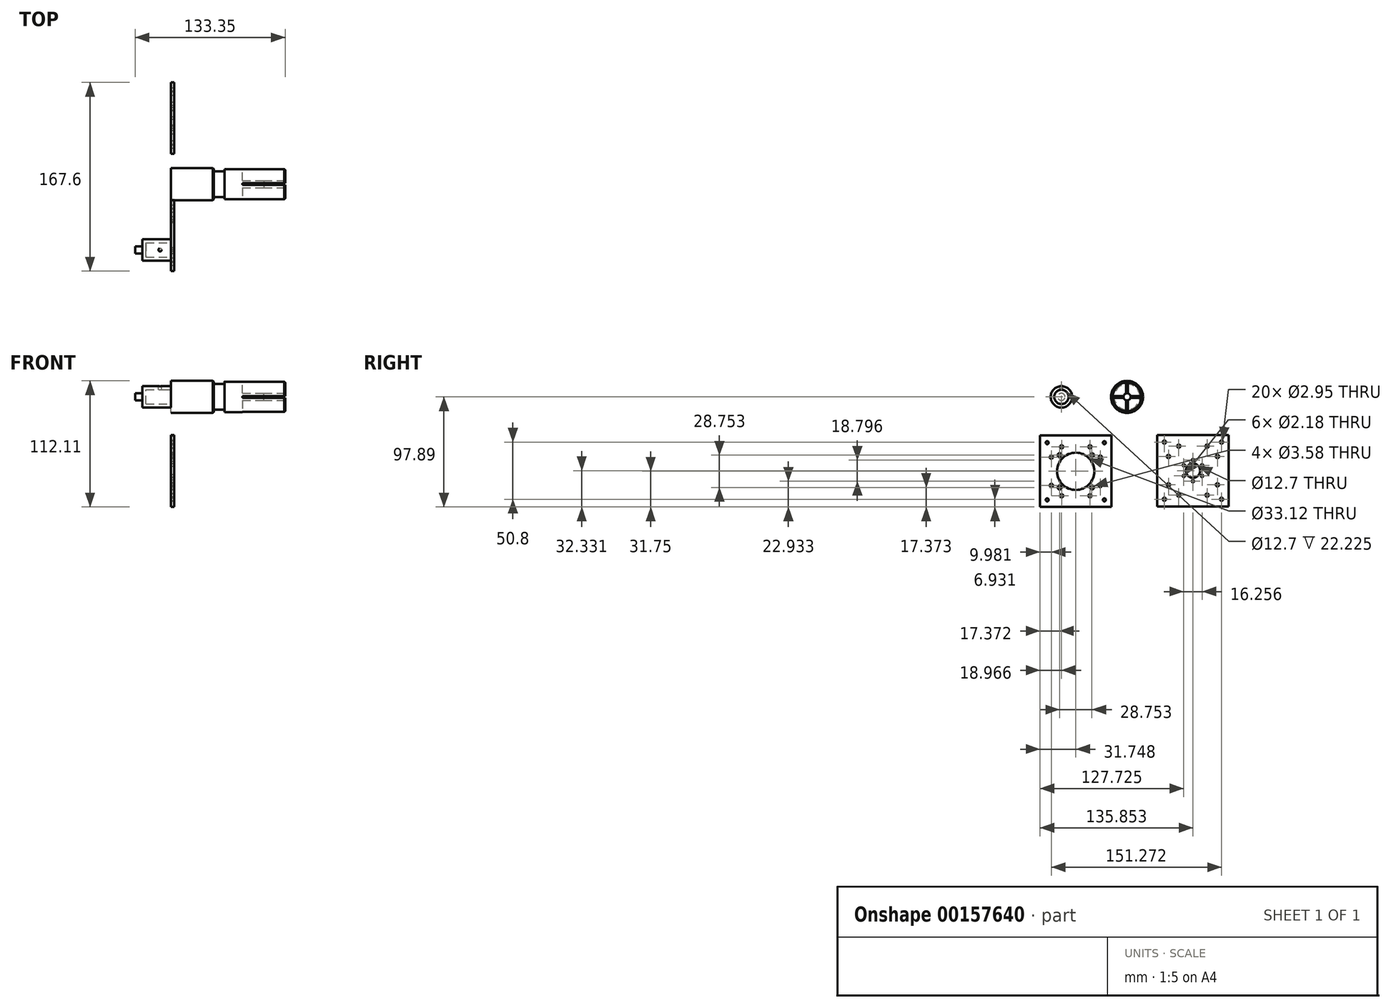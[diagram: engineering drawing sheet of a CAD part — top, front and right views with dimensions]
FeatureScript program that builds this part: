
annotation { "Feature Type Name" : "Feature", "Feature Type Description" : "" }
export const myFeature = defineFeature(function(context is Context, id is Id, definition is map)
    precondition{}
    {
        {
            var Q0;
            Q0=qCreatedBy(makeId("Right.planeOp"),FACE);
            var sketch = newSketch(context, id + "F0", { "sketchPlane" : qUnion([Q0])});
            skCircle(sketch, "E0", {"center": v(0, 0) * mm, "radius": 14.22 * mm});
            skSolve(sketch);
        }
        {
            var Q0;
            Q0=makeQuery(id+"F0.imprint","IMPRINT",FACE,{"disambiguationData":[TD([[makeQuery(id+"F0.imprint","IMPRINT",EDGE,{"derivedFrom":sQuery(id+"F0.wireOp",EDGE,"E0")}),1.0]])]});
            extrude(context, id + "F1", {"entities" : qUnion([Q0]), "depth" : 38.1 * mm});
        }
        {
            var Q0;
            Q0=makeQuery(id+"F1.opExtrude","CAP_FACE",FACE,{"disambiguationData":[OSD([sQuery(id+"F0.wireOp",EDGE,"E0")])],"isStart":false});
            var sketch = newSketch(context, id + "F2", { "sketchPlane" : qUnion([Q0])});
            skCircle(sketch, "E1", {"center": v(0, 0) * mm, "radius": 11.43 * mm});
            skSolve(sketch);
        }
        {
            var Q0;
            Q0=makeQuery(id+"F2.imprint","IMPRINT",FACE,{"disambiguationData":[TD([[makeQuery(id+"F2.imprint","IMPRINT",EDGE,{"derivedFrom":sQuery(id+"F2.wireOp",EDGE,"E1")}),1.0]])]});
            extrude(context, id + "F3", {"entities" : qUnion([Q0]), "operationType" : NewBodyOperationType.ADD, "depth" : 9.65 * mm});
        }
        {
            var Q0;
            Q0=makeQuery(id+"F3.opExtrude","CAP_FACE",FACE,{"disambiguationData":[OSD([sQuery(id+"F2.wireOp",EDGE,"E1")])],"isStart":false});
            var sketch = newSketch(context, id + "F4", { "sketchPlane" : qUnion([Q0])});
            skCircle(sketch, "E2", {"center": v(0, 0) * mm, "radius": 13.45 * mm});
            skSolve(sketch);
        }
        {
            var Q0;
            Q0=makeQuery(id+"F4.imprint","IMPRINT",FACE,{"disambiguationData":[TD([[makeQuery(id+"F4.imprint","IMPRINT",EDGE,{"derivedFrom":sQuery(id+"F4.wireOp",EDGE,"E2")}),1.0]])]});
            var Q1;
            Q1=makeQuery(id+"F4.imprint","IMPRINT",FACE,{"disambiguationData":[TD([[makeQuery(id+"F4.imprint","IMPRINT",EDGE,{"derivedFrom":makeQuery(id+"F3.opExtrude","CAP_EDGE",EDGE,{"disambiguationData":[OSD([sQuery(id+"F2.wireOp",EDGE,"E1")])],"isStart":false})}),1.0]])]});
            extrude(context, id + "F5", {"entities" : qUnion([Q0, Q1]), "operationType" : NewBodyOperationType.ADD, "depth" : 53.85 * mm});
        }
        {
            var Q0;
            Q0=makeQuery(id+"F5.opExtrude","CAP_FACE",FACE,{"disambiguationData":[OSD([sQuery(id+"F4.wireOp",EDGE,"E2")])],"isStart":false});
            var sketch = newSketch(context, id + "F6", { "sketchPlane" : qUnion([Q0])});
            skCircle(sketch, "E3", {"center": v(0, 0) * mm, "radius": 3.18 * mm});
            skSolve(sketch);
        }
        {
            var Q0;
            Q0=makeQuery(id+"F6.imprint","IMPRINT",FACE,{"disambiguationData":[TD([[makeQuery(id+"F6.imprint","IMPRINT",EDGE,{"derivedFrom":sQuery(id+"F6.wireOp",EDGE,"E3")}),1.0]])]});
            extrude(context, id + "F7", {"entities" : qUnion([Q0]), "operationType" : NewBodyOperationType.REMOVE, "oppositeDirection" : true, "depth" : 19.05 * mm});
        }
        {
            var Q0;
            Q0=makeQuery(id+"F5.opExtrude","CAP_FACE",FACE,{"disambiguationData":[OSD([sQuery(id+"F4.wireOp",EDGE,"E2")])],"isStart":false});
            var sketch = newSketch(context, id + "F8", { "sketchPlane" : qUnion([Q0])});
            skLineSegment(sketch, "E4", {"start": v(0, 0) * mm, "end": v(13.45, 0) * mm, "construction": true});
            skLineSegment(sketch, "E5", {"start": v(0, 13.45) * mm, "end": v(0, -13.45) * mm, "construction": true});
            skLineSegment(sketch, "E6", {"start": v(0, 0) * mm, "end": v(-13.45, 0) * mm, "construction": true});
            skLineSegment(sketch, "E7", {"start": v(0, 0) * mm, "end": v(0, 0.75) * mm});
            skLineSegment(sketch, "E8", {"start": v(0.77, 0.75) * mm, "end": v(13.43, 0.75) * mm});
            skLineSegment(sketch, "E9.MirrorCS", {"start": v(0.77, -0.75) * mm, "end": v(13.43, -0.75) * mm});
            skLineSegment(sketch, "E10.MirrorCS", {"start": v(-0.77, 0.75) * mm, "end": v(-13.43, 0.75) * mm});
            skLineSegment(sketch, "E11.MirrorCS", {"start": v(-0.77, -0.75) * mm, "end": v(-13.43, -0.75) * mm});
            skLineSegment(sketch, "E12", {"start": v(0, 0) * mm, "end": v(-0.77, 0) * mm});
            skLineSegment(sketch, "E13", {"start": v(-0.77, 0.75) * mm, "end": v(-0.77, 13.43) * mm});
            skLineSegment(sketch, "E14", {"start": v(-0.77, -0.75) * mm, "end": v(-0.77, -13.43) * mm});
            skLineSegment(sketch, "E15.MirrorCS", {"start": v(0.77, 0.75) * mm, "end": v(0.77, 13.43) * mm});
            skLineSegment(sketch, "E16.MirrorCS", {"start": v(0.77, -0.75) * mm, "end": v(0.77, -13.43) * mm});
            skPoint(sketch, "E17", {"position": v(-0.77, 0.75) * mm});
            skPoint(sketch, "E18", {"position": v(-0.77, -0.75) * mm});
            skPoint(sketch, "E19", {"position": v(0.77, -0.75) * mm});
            skPoint(sketch, "E20", {"position": v(0.77, 0.75) * mm});
            skPoint(sketch, "E21.orphan", {"position": v(0, 0.75) * mm});
            skPoint(sketch, "E22.orphan", {"position": v(0, -0.75) * mm});
            skPoint(sketch, "E23.orphan", {"position": v(0.77, 0) * mm});
            skSolve(sketch);
        }
        {
            var Q0;
            {var subQ0=sQuery(id+"F8.wireOp",EDGE,"E13");var subQ1=makeQuery(id+"F5.opExtrude","CAP_EDGE",EDGE,{"disambiguationData":[OSD([sQuery(id+"F4.wireOp",EDGE,"E2")])],"isStart":false});var subQ2=makeQuery(id+"F8.imprint","INTERSECT",VERTEX,{"derivedFrom":[subQ1,subQ0]});Q0=makeQuery(id+"F8.imprint","IMPRINT",FACE,{"disambiguationData":[TD([[makeQuery(id+"F8.imprint","IMPRINT",EDGE,{"disambiguationData":[TD([[subQ2,1.0]])],"derivedFrom":subQ0}),-1.0]])]});}
            var Q1;
            {var subQ0=sQuery(id+"F8.wireOp",EDGE,"E8");var subQ1=makeQuery(id+"F5.opExtrude","CAP_EDGE",EDGE,{"disambiguationData":[OSD([sQuery(id+"F4.wireOp",EDGE,"E2")])],"isStart":false});var subQ2=makeQuery(id+"F8.imprint","INTERSECT",VERTEX,{"derivedFrom":[subQ1,subQ0]});Q1=makeQuery(id+"F8.imprint","IMPRINT",FACE,{"disambiguationData":[TD([[makeQuery(id+"F8.imprint","IMPRINT",EDGE,{"disambiguationData":[TD([[subQ2,1.0]])],"derivedFrom":subQ0}),-1.0]])]});}
            var Q2;
            {var subQ0=sQuery(id+"F8.wireOp",EDGE,"E10.MirrorCS");var subQ1=makeQuery(id+"F5.opExtrude","CAP_EDGE",EDGE,{"disambiguationData":[OSD([sQuery(id+"F4.wireOp",EDGE,"E2")])],"isStart":false});var subQ2=makeQuery(id+"F8.imprint","INTERSECT",VERTEX,{"derivedFrom":[subQ1,subQ0]});Q2=makeQuery(id+"F8.imprint","IMPRINT",FACE,{"disambiguationData":[TD([[makeQuery(id+"F8.imprint","IMPRINT",EDGE,{"disambiguationData":[TD([[subQ2,1.0]])],"derivedFrom":subQ0}),1.0]])]});}
            var Q3;
            {var subQ0=sQuery(id+"F8.wireOp",EDGE,"E14");var subQ1=makeQuery(id+"F5.opExtrude","CAP_EDGE",EDGE,{"disambiguationData":[OSD([sQuery(id+"F4.wireOp",EDGE,"E2")])],"isStart":false});var subQ2=makeQuery(id+"F8.imprint","INTERSECT",VERTEX,{"derivedFrom":[subQ1,subQ0]});Q3=makeQuery(id+"F8.imprint","IMPRINT",FACE,{"disambiguationData":[TD([[makeQuery(id+"F8.imprint","IMPRINT",EDGE,{"disambiguationData":[TD([[subQ2,1.0]])],"derivedFrom":subQ0}),1.0]])]});}
            extrude(context, id + "F9", {"entities" : qUnion([Q0, Q1, Q2, Q3]), "operationType" : NewBodyOperationType.REMOVE, "oppositeDirection" : true, "depth" : 38.1 * mm});
        }
        {
            var Q0;
            {var subQ0=sQuery(id+"F4.wireOp",EDGE,"E2");Q0=makeQuery(id+"F9.boolean.opBoolean","SPLIT",EDGE,{"disambiguationData":[TD([makeQuery(id+"F9.opExtrude","SWEPT_FACE",FACE,{"disambiguationData":[OSD([sQuery(id+"F8.wireOp",EDGE,"E10.MirrorCS")])]})])],"derivedFrom":makeQuery(id+"F5.opExtrude","CAP_EDGE",EDGE,{"disambiguationData":[OSD([subQ0])],"isStart":false})});}
            var Q1;
            {var subQ0=sQuery(id+"F4.wireOp",EDGE,"E2");Q1=makeQuery(id+"F9.boolean.opBoolean","SPLIT",EDGE,{"disambiguationData":[TD([makeQuery(id+"F9.opExtrude","SWEPT_FACE",FACE,{"disambiguationData":[OSD([sQuery(id+"F8.wireOp",EDGE,"E8")])]})])],"derivedFrom":makeQuery(id+"F5.opExtrude","CAP_EDGE",EDGE,{"disambiguationData":[OSD([subQ0])],"isStart":false})});}
            var Q2;
            {var subQ0=sQuery(id+"F4.wireOp",EDGE,"E2");Q2=makeQuery(id+"F9.boolean.opBoolean","SPLIT",EDGE,{"disambiguationData":[TD([makeQuery(id+"F9.opExtrude","SWEPT_FACE",FACE,{"disambiguationData":[OSD([sQuery(id+"F8.wireOp",EDGE,"E9.MirrorCS")])]})])],"derivedFrom":makeQuery(id+"F5.opExtrude","CAP_EDGE",EDGE,{"disambiguationData":[OSD([subQ0])],"isStart":false})});}
            var Q3;
            {var subQ0=sQuery(id+"F4.wireOp",EDGE,"E2");Q3=makeQuery(id+"F9.boolean.opBoolean","SPLIT",EDGE,{"disambiguationData":[TD([makeQuery(id+"F9.opExtrude","SWEPT_FACE",FACE,{"disambiguationData":[OSD([sQuery(id+"F8.wireOp",EDGE,"E11.MirrorCS")])]})])],"derivedFrom":makeQuery(id+"F5.opExtrude","CAP_EDGE",EDGE,{"disambiguationData":[OSD([subQ0])],"isStart":false})});}
            var Q4;
            Q4=makeQuery(id+"F1.opExtrude","CAP_EDGE",EDGE,{"disambiguationData":[OSD([sQuery(id+"F0.wireOp",EDGE,"E0")])],"isStart":false});
            chamfer(context, id + "F10", {"entities" : qUnion([Q0, Q1, Q2, Q3, Q4]), "width" : 0.76 * mm, "tangentPropagation" : true});
        }
        {
            var Q0;
            Q0=qCreatedBy(makeId("Right.planeOp"),FACE);
            var sketch = newSketch(context, id + "F11", { "sketchPlane" : qUnion([Q0])});
            skLineSegment(sketch, "E24.bottom", {"start": v(-48.8, 9.53) * mm, "end": v(-67.85, 9.53) * mm});
            skLineSegment(sketch, "E24.top", {"start": v(-48.8, -9.52) * mm, "end": v(-67.85, -9.52) * mm});
            skLineSegment(sketch, "E24.left", {"start": v(-48.8, 9.53) * mm, "end": v(-48.8, -9.52) * mm});
            skLineSegment(sketch, "E24.right", {"start": v(-67.85, 9.53) * mm, "end": v(-67.85, -9.52) * mm});
            skPoint(sketch, "E24.middle", {"position": v(-58.32, 0) * mm});
            skCircle(sketch, "E25", {"center": v(-58.32, 0) * mm, "radius": 9.53 * mm});
            skSolve(sketch);
        }
        {
            var Q0;
            {var subQ0=sQuery(id+"F11.wireOp",EDGE,"E24.left");var subQ1=sQuery(id+"F11.wireOp",EDGE,"E24.bottom");var subQ2=makeQuery(id+"F11.imprint","INTERSECT",VERTEX,{"derivedFrom":[subQ1,subQ0]});Q0=makeQuery(id+"F11.imprint","IMPRINT",FACE,{"disambiguationData":[TD([[makeQuery(id+"F11.imprint","IMPRINT",EDGE,{"disambiguationData":[TD([[subQ2,-1.0]])],"derivedFrom":subQ1}),1.0]])]});}
            var Q1;
            {var subQ0=sQuery(id+"F11.wireOp",EDGE,"E25");var subQ1=makeQuery(id+"F11.imprint","INTERSECT",VERTEX,{"derivedFrom":[sQuery(id+"F11.wireOp",EDGE,"E24.bottom"),subQ0]});Q1=makeQuery(id+"F11.imprint","IMPRINT",FACE,{"disambiguationData":[TD([[makeQuery(id+"F11.imprint","IMPRINT",EDGE,{"disambiguationData":[TD([[subQ1,1.0]])],"derivedFrom":subQ0}),1.0]])]});}
            var Q2;
            {var subQ0=sQuery(id+"F11.wireOp",EDGE,"E24.left");var subQ1=sQuery(id+"F11.wireOp",EDGE,"E24.top");var subQ2=makeQuery(id+"F11.imprint","INTERSECT",VERTEX,{"derivedFrom":[subQ1,subQ0]});Q2=makeQuery(id+"F11.imprint","IMPRINT",FACE,{"disambiguationData":[TD([[makeQuery(id+"F11.imprint","IMPRINT",EDGE,{"disambiguationData":[TD([[subQ2,-1.0]])],"derivedFrom":subQ1}),-1.0]])]});}
            var Q3;
            {var subQ0=sQuery(id+"F11.wireOp",EDGE,"E24.right");var subQ1=sQuery(id+"F11.wireOp",EDGE,"E24.bottom");var subQ2=makeQuery(id+"F11.imprint","INTERSECT",VERTEX,{"derivedFrom":[subQ1,subQ0]});Q3=makeQuery(id+"F11.imprint","IMPRINT",FACE,{"disambiguationData":[TD([[makeQuery(id+"F11.imprint","IMPRINT",EDGE,{"disambiguationData":[TD([[subQ2,1.0]])],"derivedFrom":subQ1}),1.0]])]});}
            var Q4;
            {var subQ0=sQuery(id+"F11.wireOp",EDGE,"E24.right");var subQ1=sQuery(id+"F11.wireOp",EDGE,"E24.top");var subQ2=makeQuery(id+"F11.imprint","INTERSECT",VERTEX,{"derivedFrom":[subQ1,subQ0]});Q4=makeQuery(id+"F11.imprint","IMPRINT",FACE,{"disambiguationData":[TD([[makeQuery(id+"F11.imprint","IMPRINT",EDGE,{"disambiguationData":[TD([[subQ2,1.0]])],"derivedFrom":subQ1}),-1.0]])]});}
            extrude(context, id + "F12", {"entities" : qUnion([Q0, Q1, Q2, Q3, Q4]), "oppositeDirection" : true, "depth" : 25.4 * mm});
        }
        {
            var Q0;
            Q0=makeQuery(id+"F12.opExtrude","SWEPT_FACE",FACE,{"disambiguationData":[OSD([sQuery(id+"F11.wireOp",EDGE,"E24.bottom")])]});
            var sketch = newSketch(context, id + "F13", { "sketchPlane" : qUnion([Q0])});
            skCircle(sketch, "E26", {"center": v(-9.53, -58.32) * mm, "radius": 1.42 * mm});
            skPoint(sketch, "E26.centerSnap0", {"position": v(0, -58.32) * mm});
            skSolve(sketch);
        }
        {
            var Q0;
            Q0=makeQuery(id+"F13.imprint","IMPRINT",FACE,{"disambiguationData":[TD([[makeQuery(id+"F13.imprint","IMPRINT",EDGE,{"derivedFrom":sQuery(id+"F13.wireOp",EDGE,"E26")}),1.0]])]});
            extrude(context, id + "F14", {"entities" : qUnion([Q0]), "operationType" : NewBodyOperationType.REMOVE, "oppositeDirection" : true, "depth" : 9.52 * mm});
        }
        {
            var Q0;
            {var subQ0=sQuery(id+"F11.wireOp",EDGE,"E24.right");var subQ1=sQuery(id+"F11.wireOp",EDGE,"E24.bottom");var subQ2=makeQuery(id+"F11.imprint","INTERSECT",VERTEX,{"derivedFrom":[subQ1,subQ0]});Q0=makeQuery(id+"F11.imprint","IMPRINT",FACE,{"disambiguationData":[TD([[makeQuery(id+"F11.imprint","IMPRINT",EDGE,{"disambiguationData":[TD([[subQ2,1.0]])],"derivedFrom":subQ1}),1.0]])]});}
            var Q1;
            {var subQ0=sQuery(id+"F11.wireOp",EDGE,"E24.left");var subQ1=sQuery(id+"F11.wireOp",EDGE,"E24.bottom");var subQ2=makeQuery(id+"F11.imprint","INTERSECT",VERTEX,{"derivedFrom":[subQ1,subQ0]});Q1=makeQuery(id+"F11.imprint","IMPRINT",FACE,{"disambiguationData":[TD([[makeQuery(id+"F11.imprint","IMPRINT",EDGE,{"disambiguationData":[TD([[subQ2,-1.0]])],"derivedFrom":subQ1}),1.0]])]});}
            var Q2;
            {var subQ0=sQuery(id+"F11.wireOp",EDGE,"E24.left");var subQ1=sQuery(id+"F11.wireOp",EDGE,"E24.top");var subQ2=makeQuery(id+"F11.imprint","INTERSECT",VERTEX,{"derivedFrom":[subQ1,subQ0]});Q2=makeQuery(id+"F11.imprint","IMPRINT",FACE,{"disambiguationData":[TD([[makeQuery(id+"F11.imprint","IMPRINT",EDGE,{"disambiguationData":[TD([[subQ2,-1.0]])],"derivedFrom":subQ1}),-1.0]])]});}
            var Q3;
            {var subQ0=sQuery(id+"F11.wireOp",EDGE,"E24.right");var subQ1=sQuery(id+"F11.wireOp",EDGE,"E24.top");var subQ2=makeQuery(id+"F11.imprint","INTERSECT",VERTEX,{"derivedFrom":[subQ1,subQ0]});Q3=makeQuery(id+"F11.imprint","IMPRINT",FACE,{"disambiguationData":[TD([[makeQuery(id+"F11.imprint","IMPRINT",EDGE,{"disambiguationData":[TD([[subQ2,1.0]])],"derivedFrom":subQ1}),-1.0]])]});}
            extrude(context, id + "F15", {"entities" : qUnion([Q0, Q1, Q2, Q3]), "operationType" : NewBodyOperationType.REMOVE, "oppositeDirection" : true, "depth" : 25.4 * mm});
        }
        {
            var Q0;
            Q0=makeQuery(id+"F12.opExtrude","CAP_FACE",FACE,{"disambiguationData":[OSD([sQuery(id+"F11.wireOp",EDGE,"E24.bottom"),sQuery(id+"F11.wireOp",EDGE,"E24.top"),sQuery(id+"F11.wireOp",EDGE,"E24.left"),sQuery(id+"F11.wireOp",EDGE,"E24.right")])],"isStart":true});
            var sketch = newSketch(context, id + "F16", { "sketchPlane" : qUnion([Q0])});
            skCircle(sketch, "E27", {"center": v(-58.32, 0) * mm, "radius": 6.35 * mm});
            skSolve(sketch);
        }
        {
            var Q0;
            Q0=makeQuery(id+"F16.imprint","IMPRINT",FACE,{"disambiguationData":[TD([[makeQuery(id+"F16.imprint","IMPRINT",EDGE,{"derivedFrom":sQuery(id+"F16.wireOp",EDGE,"E27")}),1.0]])]});
            extrude(context, id + "F17", {"entities" : qUnion([Q0]), "operationType" : NewBodyOperationType.REMOVE, "oppositeDirection" : true, "depth" : 22.22 * mm});
        }
        {
            var Q0;
            Q0=makeQuery(id+"F12.opExtrude","CAP_FACE",FACE,{"disambiguationData":[OSD([sQuery(id+"F11.wireOp",EDGE,"E24.bottom"),sQuery(id+"F11.wireOp",EDGE,"E24.top"),sQuery(id+"F11.wireOp",EDGE,"E24.left"),sQuery(id+"F11.wireOp",EDGE,"E24.right")])],"isStart":false});
            var sketch = newSketch(context, id + "F18", { "sketchPlane" : qUnion([Q0])});
            skCircle(sketch, "E28", {"center": v(58.32, 0) * mm, "radius": 3.18 * mm});
            skSolve(sketch);
        }
        {
            var Q0;
            Q0=makeQuery(id+"F18.imprint","IMPRINT",FACE,{"disambiguationData":[TD([[makeQuery(id+"F18.imprint","IMPRINT",EDGE,{"derivedFrom":sQuery(id+"F18.wireOp",EDGE,"E28")}),1.0]])]});
            extrude(context, id + "F19", {"entities" : qUnion([Q0]), "operationType" : NewBodyOperationType.ADD, "depth" : 6.35 * mm});
        }
        {
            var Q0;
            Q0=qCreatedBy(makeId("Right.planeOp"),FACE);
            var sketch = newSketch(context, id + "F20", { "sketchPlane" : qUnion([Q0])});
            skLineSegment(sketch, "E29.bottom", {"start": v(-77.3, -34.4) * mm, "end": v(-13.8, -34.4) * mm});
            skLineSegment(sketch, "E29.top", {"start": v(-77.3, -97.9) * mm, "end": v(-13.8, -97.9) * mm});
            skLineSegment(sketch, "E29.left", {"start": v(-77.3, -34.4) * mm, "end": v(-77.3, -97.9) * mm});
            skLineSegment(sketch, "E29.right", {"start": v(-13.8, -34.4) * mm, "end": v(-13.8, -97.9) * mm});
            skCircle(sketch, "E30", {"center": v(-20.14, -40.74) * mm, "radius": 1.35 * mm});
            skLineSegment(sketch, "E31", {"start": v(-45.54, -34.4) * mm, "end": v(-45.54, -97.9) * mm, "construction": true});
            skLineSegment(sketch, "E32", {"start": v(-77.3, -66.14) * mm, "end": v(-13.8, -66.14) * mm, "construction": true});
            skCircle(sketch, "E33.MirrorC", {"center": v(-70.94, -40.74) * mm, "radius": 1.35 * mm});
            skLineSegment(sketch, "E34.MirrorCS", {"start": v(-13.8, -66.14) * mm, "end": v(-77.3, -66.14) * mm, "construction": true});
            skCircle(sketch, "E35.MirrorC", {"center": v(-70.94, -91.54) * mm, "radius": 1.35 * mm});
            skCircle(sketch, "E36.MirrorC", {"center": v(-20.14, -91.54) * mm, "radius": 1.35 * mm});
            skCircle(sketch, "E37", {"center": v(-32.97, -44.37) * mm, "radius": 1.47 * mm});
            skCircle(sketch, "E38", {"center": v(-31.17, -51.76) * mm, "radius": 1.8 * mm});
            skCircle(sketch, "E39.MirrorC", {"center": v(-58.11, -44.37) * mm, "radius": 1.47 * mm});
            skCircle(sketch, "E40.MirrorC", {"center": v(-59.92, -51.76) * mm, "radius": 1.8 * mm});
            skCircle(sketch, "E41.MirrorC", {"center": v(-59.92, -80.52) * mm, "radius": 1.8 * mm});
            skCircle(sketch, "E42.MirrorC", {"center": v(-58.11, -87.9) * mm, "radius": 1.47 * mm});
            skCircle(sketch, "E43.MirrorC", {"center": v(-32.97, -87.9) * mm, "radius": 1.47 * mm});
            skCircle(sketch, "E44.MirrorC", {"center": v(-31.17, -80.52) * mm, "radius": 1.8 * mm});
            skCircle(sketch, "E45", {"center": v(-23.77, -53.57) * mm, "radius": 1.47 * mm});
            skCircle(sketch, "E46.MirrorC", {"center": v(-67.3, -53.57) * mm, "radius": 1.47 * mm});
            skCircle(sketch, "E47.MirrorC", {"center": v(-67.3, -78.71) * mm, "radius": 1.47 * mm});
            skCircle(sketch, "E48.MirrorC", {"center": v(-23.77, -78.71) * mm, "radius": 1.47 * mm});
            skCircle(sketch, "E49", {"center": v(-45.54, -66.14) * mm, "radius": 16.56 * mm});
            skSolve(sketch);
        }
        {
            var Q0;
            Q0=makeQuery(id+"F20.imprint","IMPRINT",FACE,{"disambiguationData":[TD([[makeQuery(id+"F20.imprint","IMPRINT",EDGE,{"derivedFrom":sQuery(id+"F20.wireOp",EDGE,"E29.bottom")}),-1.0]])]});
            extrude(context, id + "F21", {"entities" : qUnion([Q0]), "depth" : 3.17 * mm});
        }
        {
            var Q0;
            Q0=qCreatedBy(makeId("Right.planeOp"),FACE);
            var sketch = newSketch(context, id + "F22", { "sketchPlane" : qUnion([Q0])});
            skLineSegment(sketch, "E50.bottom", {"start": v(26.81, -33.8) * mm, "end": v(90.31, -33.8) * mm});
            skLineSegment(sketch, "E50.top", {"start": v(26.81, -97.3) * mm, "end": v(90.31, -97.3) * mm});
            skLineSegment(sketch, "E50.left", {"start": v(26.81, -33.8) * mm, "end": v(26.81, -97.3) * mm});
            skLineSegment(sketch, "E50.right", {"start": v(90.31, -33.8) * mm, "end": v(90.31, -97.3) * mm});
            skLineSegment(sketch, "E51", {"start": v(58.56, -33.8) * mm, "end": v(58.56, -97.3) * mm, "construction": true});
            skLineSegment(sketch, "E52", {"start": v(26.81, -65.56) * mm, "end": v(90.31, -65.56) * mm, "construction": true});
            skCircle(sketch, "E53", {"center": v(71.14, -43.8) * mm, "radius": 1.47 * mm});
            skCircle(sketch, "E54", {"center": v(80.33, -52.99) * mm, "radius": 1.47 * mm});
            skCircle(sketch, "E55.MirrorC", {"center": v(71.14, -87.33) * mm, "radius": 1.47 * mm});
            skCircle(sketch, "E56.MirrorC", {"center": v(80.33, -78.13) * mm, "radius": 1.47 * mm});
            skCircle(sketch, "E57.MirrorC", {"center": v(46, -43.8) * mm, "radius": 1.47 * mm});
            skCircle(sketch, "E58.MirrorC", {"center": v(36.8, -52.99) * mm, "radius": 1.47 * mm});
            skCircle(sketch, "E59.MirrorC", {"center": v(36.8, -78.13) * mm, "radius": 1.47 * mm});
            skCircle(sketch, "E60.MirrorC", {"center": v(46, -87.33) * mm, "radius": 1.47 * mm});
            skCircle(sketch, "E61", {"center": v(58.56, -65.56) * mm, "radius": 6.35 * mm});
            skCircle(sketch, "E62", {"center": v(66.7, -60.86) * mm, "radius": 1.1 * mm});
            skCircle(sketch, "E63", {"center": v(58.56, -56.16) * mm, "radius": 1.1 * mm});
            skCircle(sketch, "E64.MirrorC", {"center": v(50.44, -60.86) * mm, "radius": 1.1 * mm});
            skCircle(sketch, "E65.MirrorC", {"center": v(66.7, -70.26) * mm, "radius": 1.1 * mm});
            skCircle(sketch, "E66.MirrorC", {"center": v(58.56, -74.96) * mm, "radius": 1.1 * mm});
            skCircle(sketch, "E67.MirrorC", {"center": v(50.44, -70.26) * mm, "radius": 1.1 * mm});
            skCircle(sketch, "E68", {"center": v(83.96, -40.16) * mm, "radius": 1.47 * mm});
            skCircle(sketch, "E69.MirrorC", {"center": v(33.16, -40.16) * mm, "radius": 1.47 * mm});
            skCircle(sketch, "E70.MirrorC", {"center": v(33.16, -90.96) * mm, "radius": 1.47 * mm});
            skCircle(sketch, "E71.MirrorC", {"center": v(83.96, -90.96) * mm, "radius": 1.47 * mm});
            skSolve(sketch);
        }
        {
            var Q0;
            Q0=makeQuery(id+"F22.imprint","IMPRINT",FACE,{"disambiguationData":[TD([[makeQuery(id+"F22.imprint","IMPRINT",EDGE,{"derivedFrom":sQuery(id+"F22.wireOp",EDGE,"E50.bottom")}),-1.0]])]});
            extrude(context, id + "F23", {"entities" : qUnion([Q0]), "depth" : 3.17 * mm});
        }
    });
